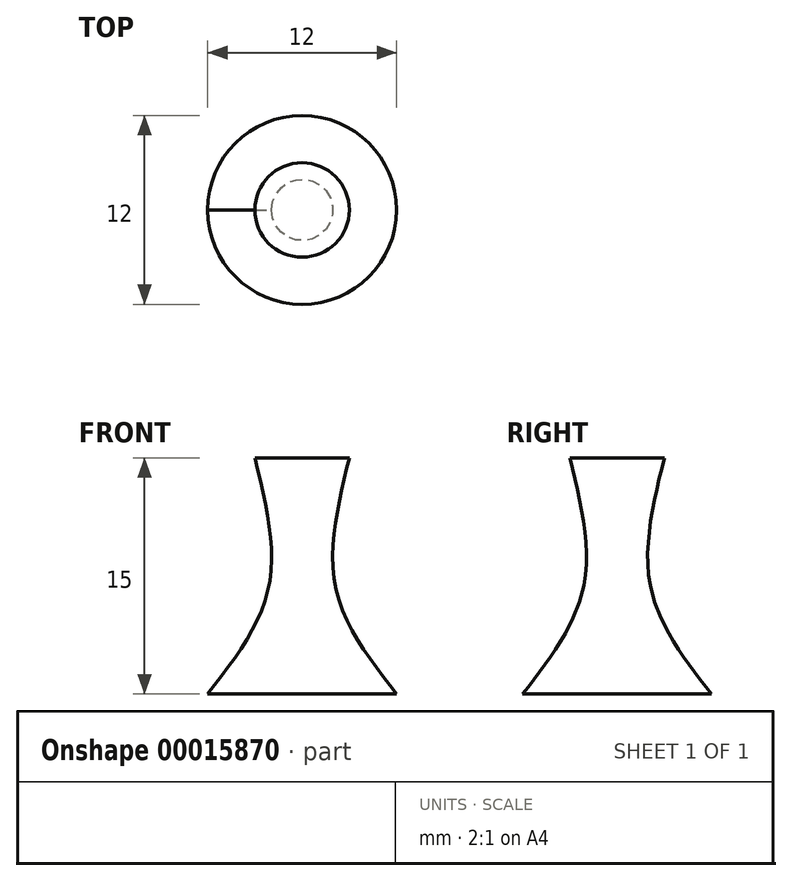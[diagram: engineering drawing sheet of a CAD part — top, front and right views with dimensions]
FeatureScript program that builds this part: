
annotation { "Feature Type Name" : "Feature", "Feature Type Description" : "" }
export const myFeature = defineFeature(function(context is Context, id is Id, definition is map)
    precondition{}
    {
        {
            var Q0;
            Q0=qCreatedBy(makeId("Front.planeOp"),FACE);
            var sketch = newSketch(context, id + "F0", { "sketchPlane" : qUnion([Q0])});
            skLineSegment(sketch, "E0", {"start": v(0, 0) * mm, "end": v(0, 15) * mm});
            skLineSegment(sketch, "E1", {"start": v(0, 15) * mm, "end": v(3, 15) * mm});
            skLineSegment(sketch, "E2", {"start": v(0, 0) * mm, "end": v(6, 0) * mm});
            skFitSpline(sketch, "E3", {"points": [v(6, 0) * mm, v(2.14, 6.75) * mm, v(3, 15) * mm], "startDerivative": vector(-10.2, 13.1) * mm, "endDerivative": vector(4.13, 16.88) * mm});
            skSolve(sketch);
        }
        {
            var Q0;
            Q0 = qSketchRegion(id + "F0", true);
            var Q1;
            Q1=sQuery(id+"F0.wireOp",EDGE,"E0");
            revolve(context, id + "F1", {"entities" : qUnion([Q0]), "axis" : qUnion([Q1]), "revolveType" : RevolveType.FULL});
        }
    });
